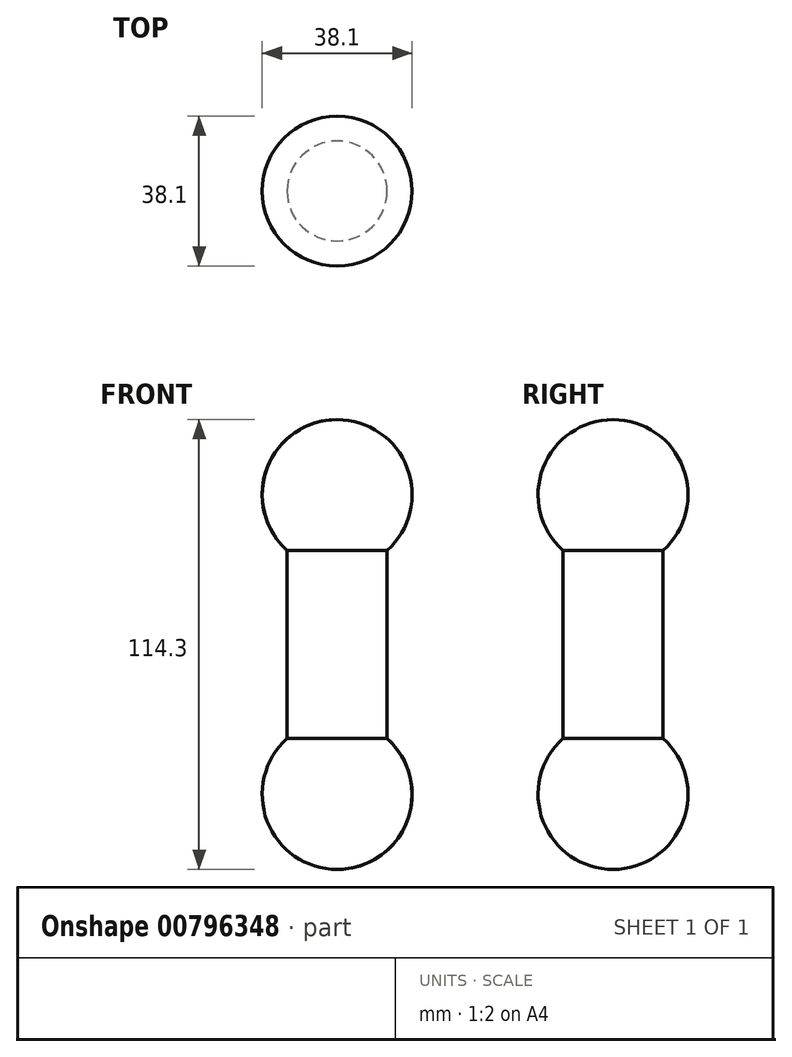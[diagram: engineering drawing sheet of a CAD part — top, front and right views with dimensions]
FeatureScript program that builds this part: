
annotation { "Feature Type Name" : "Feature", "Feature Type Description" : "" }
export const myFeature = defineFeature(function(context is Context, id is Id, definition is map)
    precondition{}
    {
        {
            var Q0;
            Q0=qCreatedBy(makeId("Top.planeOp"),FACE);
            var sketch = newSketch(context, id + "F0", { "sketchPlane" : qUnion([Q0])});
            skCircle(sketch, "E0", {"center": v(0, 0) * mm, "radius": 12.7 * mm});
            skSolve(sketch);
        }
        {
            var Q0;
            Q0=makeQuery(id+"F0.imprint","IMPRINT",FACE,{"disambiguationData":[TD([[makeQuery(id+"F0.imprint","IMPRINT",EDGE,{"derivedFrom":sQuery(id+"F0.wireOp",EDGE,"E0")}),1.0]])]});
            extrude(context, id + "F1", {"entities" : qUnion([Q0]), "depth" : 76.2 * mm, "offsetDistance" : 25.4 * mm});
        }
        {
            var Q0;
            Q0=qCreatedBy(makeId("Front.planeOp"),FACE);
            var sketch = newSketch(context, id + "F2", { "sketchPlane" : qUnion([Q0])});
            skLineSegment(sketch, "E1.0", {"start": v(-12.7, 76.2) * mm, "end": v(12.7, 76.2) * mm});
            skLineSegment(sketch, "E2", {"start": v(0, 95.25) * mm, "end": v(0, 76.2) * mm});
            skArc(sketch, "E3", {"start": v(0, 95.25) * mm, "mid": v(19.05, 76.2) * mm, "end": v(0, 57.15) * mm});
            skLineSegment(sketch, "E4", {"start": v(0, 76.2) * mm, "end": v(0, 57.15) * mm});
            skSolve(sketch);
        }
        {
            var Q0;
            Q0=makeQuery(id+"F2.imprint","IMPRINT",FACE,{"disambiguationData":[TD([[makeQuery(id+"F2.imprint","IMPRINT",EDGE,{"derivedFrom":sQuery(id+"F2.wireOp",EDGE,"E2")}),1.0]])]});
            var Q1;
            Q1=sQuery(id+"F2.wireOp",EDGE,"E2");
            revolve(context, id + "F3", {"operationType" : NewBodyOperationType.ADD, "surfaceOperationType" : NewSurfaceOperationType.NEW, "entities" : qUnion([Q0]), "axis" : qUnion([Q1]), "revolveType" : RevolveType.FULL});
        }
        {
            var Q0;
            Q0=qCreatedBy(makeId("Front.planeOp"),FACE);
            var sketch = newSketch(context, id + "F4", { "sketchPlane" : qUnion([Q0])});
            skLineSegment(sketch, "E5.0.0", {"start": v(12.7, 0) * mm, "end": v(-12.7, 0) * mm});
            skLineSegment(sketch, "E6", {"start": v(0, -19.05) * mm, "end": v(0, 0) * mm});
            skLineSegment(sketch, "E7", {"start": v(0, 0) * mm, "end": v(12.7, 0) * mm});
            skArc(sketch, "E8", {"start": v(0, -19.05) * mm, "mid": v(19.05, 0) * mm, "end": v(0, 19.05) * mm});
            skLineSegment(sketch, "E9", {"start": v(0, 19.05) * mm, "end": v(0, 0) * mm});
            skSolve(sketch);
        }
        {
            var Q0;
            Q0=makeQuery(id+"F4.imprint","IMPRINT",FACE,{"disambiguationData":[TD([[makeQuery(id+"F4.imprint","IMPRINT",EDGE,{"derivedFrom":sQuery(id+"F4.wireOp",EDGE,"E6")}),-1.0]])]});
            var Q1;
            Q1=sQuery(id+"F4.wireOp",EDGE,"E6");
            revolve(context, id + "F5", {"operationType" : NewBodyOperationType.ADD, "surfaceOperationType" : NewSurfaceOperationType.NEW, "entities" : qUnion([Q0]), "axis" : qUnion([Q1]), "revolveType" : RevolveType.FULL});
        }
    });
